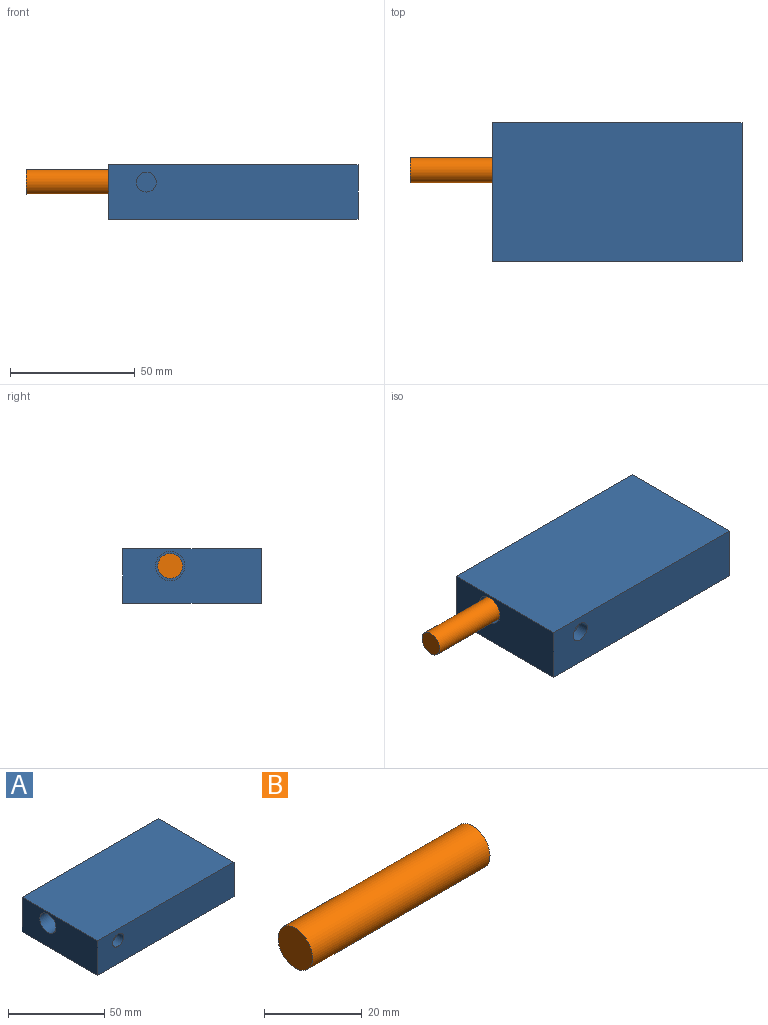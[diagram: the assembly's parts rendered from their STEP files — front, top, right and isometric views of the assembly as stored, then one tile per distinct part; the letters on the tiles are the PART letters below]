
ASSEMBLY  parts=2 mates=1
PART A: 10 faces, bbox 100x55.5x22 mm
  f0: plane 100x55.5mm, normal (0,0,1), area 5550mm2, adj f1,f3,f4,f5
  f1: plane 55.5x22mm, normal (-1,0,0), area 1111.8mm2, adj f0,f2,f3,f4,f8
  f2: plane 100x55.5mm, normal (0,0,-1), area 5550mm2, adj f1,f3,f4,f5
  f3: plane 100x22mm, normal (0,1,0), area 2200mm2, adj f0,f1,f2,f5
  f4: plane 100x22mm, normal (0,-1,0), area 2149.7mm2, adj f0,f1,f2,f5,f6
  f5: plane 55.5x22mm, normal (1,0,0), area 1221mm2, adj f0,f2,f3,f4
  f6: cylinder r=4mm len=8mm, axis (0,-1,0), area 125.7mm2, adj f4,f7
  f7: plane 8x8mm, normal (0,-1,0), area 50.3mm2, adj f6
  f8: cylinder r=5.9mm len=18mm, axis (-1,0,0), area 666.8mm2, adj f1,f9
  f9: plane 11.79x11.79mm, normal (-1,0,0), area 109.2mm2, adj f8
PART B: 3 faces, bbox 51.3x10x10 mm
  f0: cylinder r=5mm len=51.3mm, axis (-1,0,0), area 1611.6mm2, adj f1,f2
  f1: plane 10x10mm, normal (1,0,0), area 78.5mm2, adj f0
  f2: plane 10x10mm, normal (-1,0,0), area 78.5mm2, adj f0
PLACE A t=(4.79,59.38,27.09)mm
PLACE B rot(axis=(0,1,0),180deg) t=(-28.94,40.38,42.09)mm
MATE planar B.f0 <-> A.f8  axis (1,0,0) through (-28.94,40.38,42.09)mm
